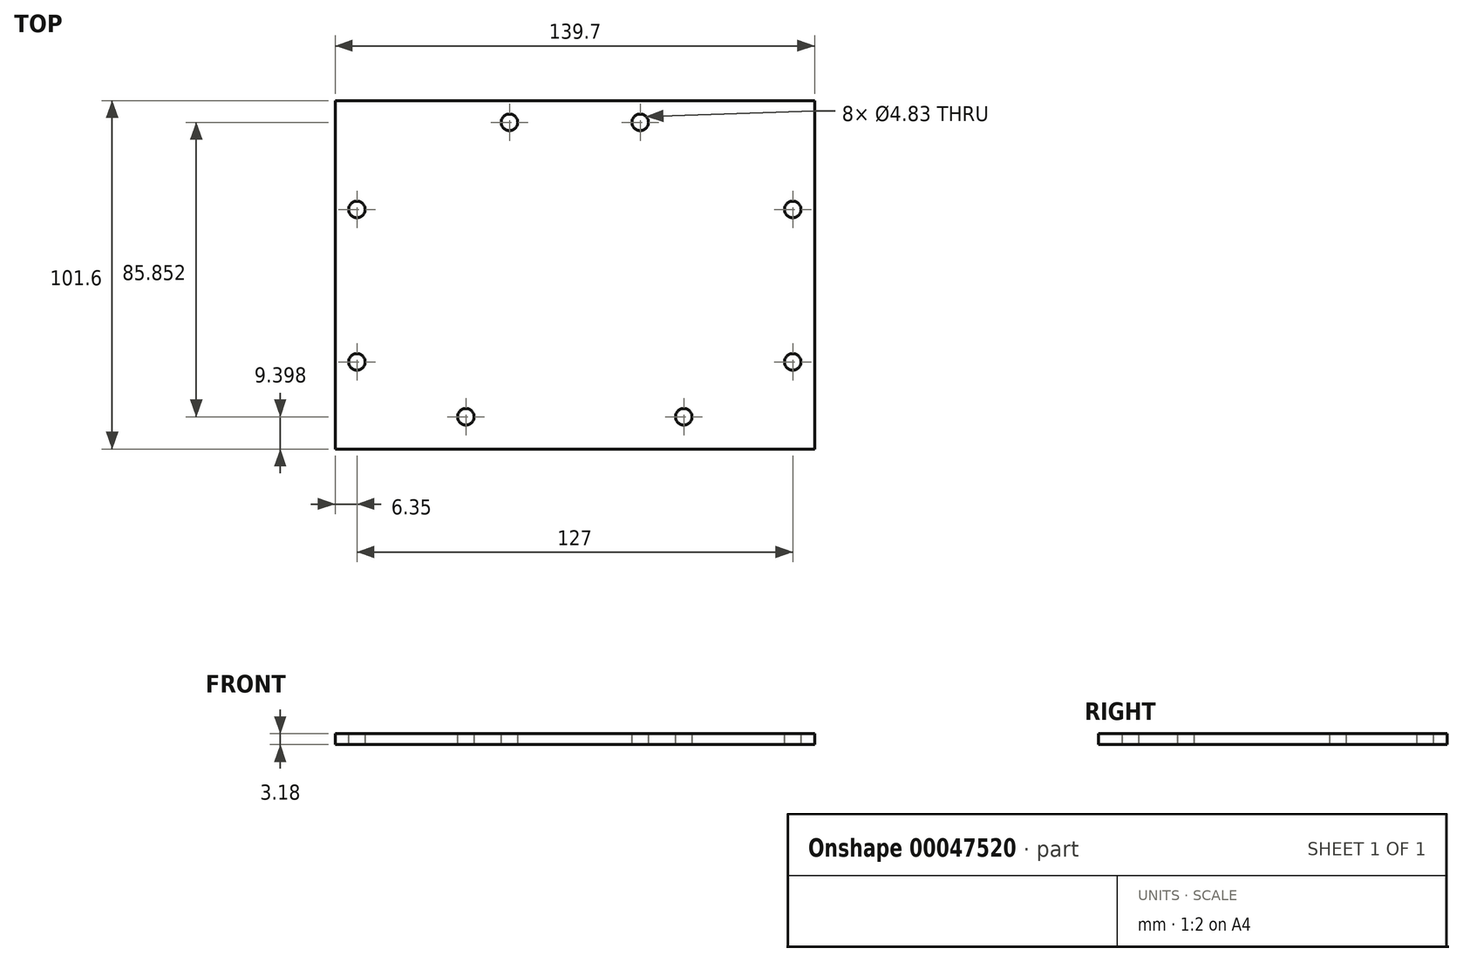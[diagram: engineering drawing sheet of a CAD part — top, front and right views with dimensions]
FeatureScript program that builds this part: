
annotation { "Feature Type Name" : "Feature", "Feature Type Description" : "" }
export const myFeature = defineFeature(function(context is Context, id is Id, definition is map)
    precondition{}
    {
        {
            var Q0;
            Q0=qCreatedBy(makeId("Top.planeOp"),FACE);
            var sketch = newSketch(context, id + "F0", { "sketchPlane" : qUnion([Q0])});
            skLineSegment(sketch, "E0.rect.bottom", {"start": v(-69.85, 50.8) * mm, "end": v(69.85, 50.8) * mm});
            skLineSegment(sketch, "E0.rect.top", {"start": v(-69.85, -50.8) * mm, "end": v(69.85, -50.8) * mm});
            skLineSegment(sketch, "E0.rect.left", {"start": v(-69.85, 50.8) * mm, "end": v(-69.85, -50.8) * mm});
            skLineSegment(sketch, "E0.rect.right", {"start": v(69.85, 50.8) * mm, "end": v(69.85, -50.8) * mm});
            skPoint(sketch, "E0.rect.middle", {"position": v(0, 0) * mm});
            skSolve(sketch);
        }
        {
            var Q0;
            Q0 = qSketchRegion(id + "F0", true);
            extrude(context, id + "F1", {"entities" : qUnion([Q0]), "endBound" : BoundingType.SYMMETRIC, "depth" : 3.17 * mm});
        }
        {
            var Q0;
            Q0=qCreatedBy(makeId("Top.planeOp"),FACE);
            var sketch = newSketch(context, id + "F2", { "sketchPlane" : qUnion([Q0])});
            skCircle(sketch, "E1", {"center": v(-63.5, 19.05) * mm, "radius": 2.41 * mm});
            skSolve(sketch);
        }
        {
            var Q0;
            Q0 = qSketchRegion(id + "F2", true);
            extrude(context, id + "F3", {"entities" : qUnion([Q0]), "operationType" : NewBodyOperationType.REMOVE, "endBound" : BoundingType.SYMMETRIC, "oppositeDirection" : true, "depth" : 3.17 * mm});
        }
        {
            var Q0;
            Q0=qCreatedBy(makeId("Top.planeOp"),FACE);
            var sketch = newSketch(context, id + "F4", { "sketchPlane" : qUnion([Q0])});
            skCircle(sketch, "E2", {"center": v(-63.5, -25.4) * mm, "radius": 2.41 * mm});
            skSolve(sketch);
        }
        {
            var Q0;
            Q0 = qSketchRegion(id + "F4", true);
            extrude(context, id + "F5", {"entities" : qUnion([Q0]), "operationType" : NewBodyOperationType.REMOVE, "endBound" : BoundingType.SYMMETRIC, "depth" : 3.17 * mm});
        }
        {
            var Q0;
            Q0=qCreatedBy(makeId("Top.planeOp"),FACE);
            var sketch = newSketch(context, id + "F6", { "sketchPlane" : qUnion([Q0])});
            skCircle(sketch, "E3", {"center": v(63.5, -25.4) * mm, "radius": 2.41 * mm});
            skSolve(sketch);
        }
        {
            var Q0;
            Q0 = qSketchRegion(id + "F6", true);
            extrude(context, id + "F7", {"entities" : qUnion([Q0]), "operationType" : NewBodyOperationType.REMOVE, "endBound" : BoundingType.SYMMETRIC, "oppositeDirection" : true, "depth" : 3.17 * mm});
        }
        {
            var Q0;
            Q0=qCreatedBy(makeId("Top.planeOp"),FACE);
            var sketch = newSketch(context, id + "F8", { "sketchPlane" : qUnion([Q0])});
            skCircle(sketch, "E4", {"center": v(63.5, 19.05) * mm, "radius": 2.41 * mm});
            skSolve(sketch);
        }
        {
            var Q0;
            Q0 = qSketchRegion(id + "F8", true);
            extrude(context, id + "F9", {"entities" : qUnion([Q0]), "operationType" : NewBodyOperationType.REMOVE, "endBound" : BoundingType.SYMMETRIC, "oppositeDirection" : true, "depth" : 3.17 * mm});
        }
        {
            var Q0;
            Q0=qCreatedBy(makeId("Top.planeOp"),FACE);
            var sketch = newSketch(context, id + "F10", { "sketchPlane" : qUnion([Q0])});
            skCircle(sketch, "E5", {"center": v(19.05, 44.45) * mm, "radius": 2.41 * mm});
            skSolve(sketch);
        }
        {
            var Q0;
            Q0 = qSketchRegion(id + "F10", true);
            extrude(context, id + "F11", {"entities" : qUnion([Q0]), "operationType" : NewBodyOperationType.REMOVE, "endBound" : BoundingType.SYMMETRIC, "oppositeDirection" : true, "depth" : 3.17 * mm});
        }
        {
            var Q0;
            Q0=qCreatedBy(makeId("Top.planeOp"),FACE);
            var sketch = newSketch(context, id + "F12", { "sketchPlane" : qUnion([Q0])});
            skCircle(sketch, "E6", {"center": v(-19.05, 44.45) * mm, "radius": 2.41 * mm});
            skSolve(sketch);
        }
        {
            var Q0;
            Q0 = qSketchRegion(id + "F12", true);
            extrude(context, id + "F13", {"entities" : qUnion([Q0]), "operationType" : NewBodyOperationType.REMOVE, "endBound" : BoundingType.SYMMETRIC, "oppositeDirection" : true, "depth" : 3.17 * mm});
        }
        {
            var Q0;
            Q0=qCreatedBy(makeId("Top.planeOp"),FACE);
            var sketch = newSketch(context, id + "F14", { "sketchPlane" : qUnion([Q0])});
            skCircle(sketch, "E7", {"center": v(31.75, -41.4) * mm, "radius": 2.41 * mm});
            skSolve(sketch);
        }
        {
            var Q0;
            Q0 = qSketchRegion(id + "F14", true);
            extrude(context, id + "F15", {"entities" : qUnion([Q0]), "operationType" : NewBodyOperationType.REMOVE, "endBound" : BoundingType.SYMMETRIC, "oppositeDirection" : true, "depth" : 3.17 * mm});
        }
        {
            var Q0;
            Q0=qCreatedBy(makeId("Top.planeOp"),FACE);
            var sketch = newSketch(context, id + "F16", { "sketchPlane" : qUnion([Q0])});
            skCircle(sketch, "E8", {"center": v(-31.75, -41.4) * mm, "radius": 2.41 * mm});
            skSolve(sketch);
        }
        {
            var Q0;
            Q0 = qSketchRegion(id + "F16", true);
            extrude(context, id + "F17", {"entities" : qUnion([Q0]), "operationType" : NewBodyOperationType.REMOVE, "endBound" : BoundingType.SYMMETRIC, "oppositeDirection" : true, "depth" : 3.17 * mm});
        }
    });
